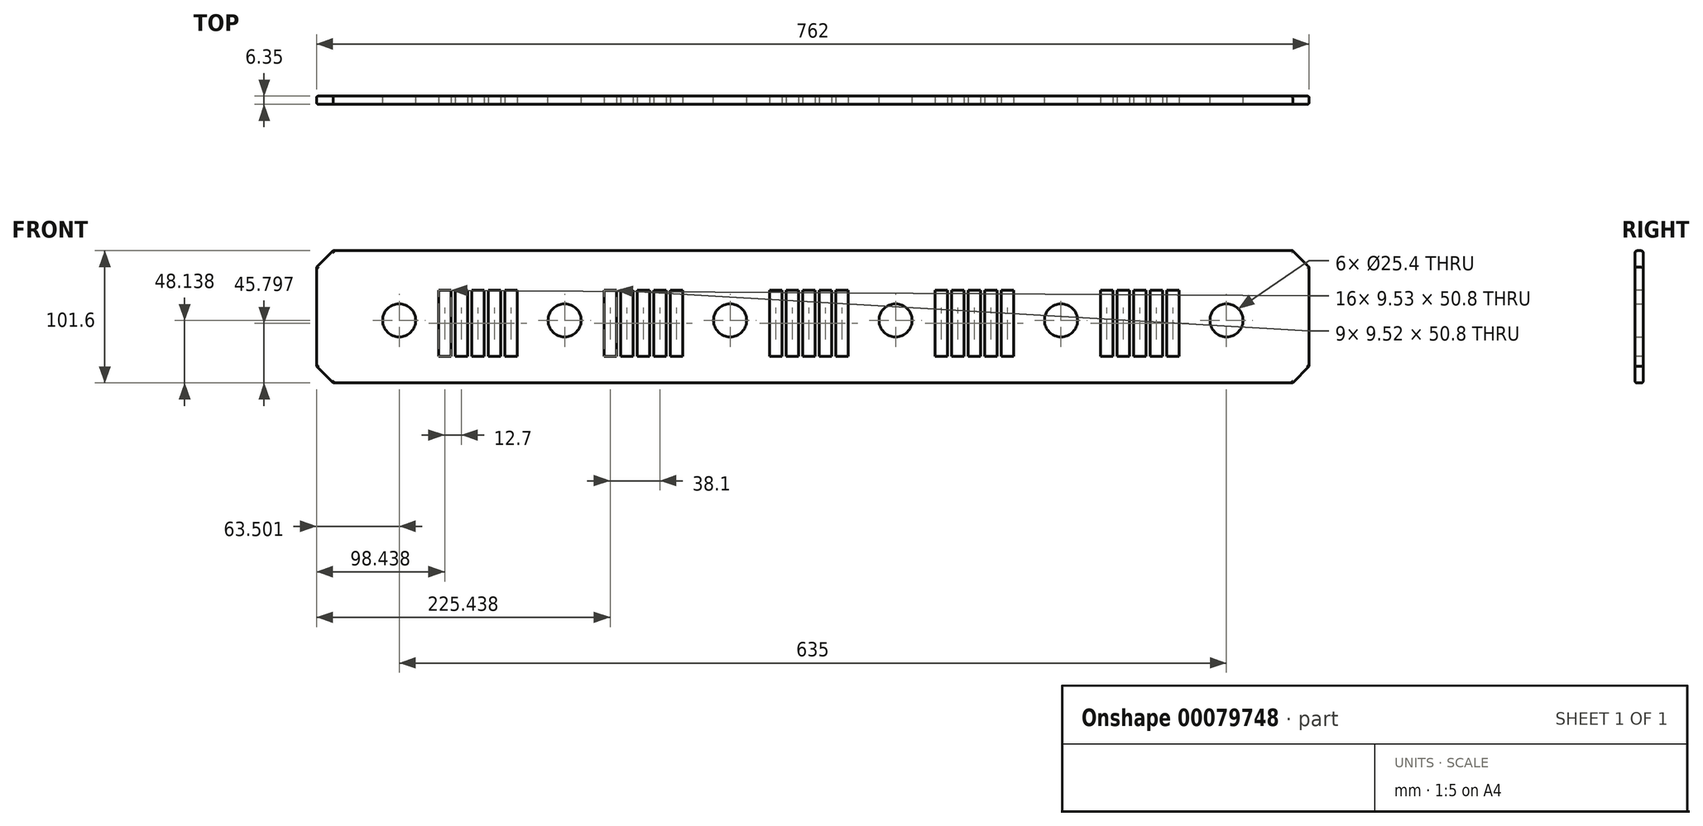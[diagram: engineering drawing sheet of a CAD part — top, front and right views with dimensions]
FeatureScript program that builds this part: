
annotation { "Feature Type Name" : "Feature", "Feature Type Description" : "" }
export const myFeature = defineFeature(function(context is Context, id is Id, definition is map)
    precondition{}
    {
        {
            var Q0;
            Q0=qCreatedBy(makeId("Front.planeOp"),FACE);
            var sketch = newSketch(context, id + "F0", { "sketchPlane" : qUnion([Q0])});
            skLineSegment(sketch, "E0.bottom", {"start": v(-361.59, -20.97) * mm, "end": v(400.41, -20.97) * mm});
            skLineSegment(sketch, "E0.top", {"start": v(-361.59, -122.57) * mm, "end": v(400.41, -122.57) * mm});
            skLineSegment(sketch, "E0.left", {"start": v(-361.59, -20.97) * mm, "end": v(-361.59, -122.57) * mm});
            skLineSegment(sketch, "E0.right", {"start": v(400.41, -20.97) * mm, "end": v(400.41, -122.57) * mm});
            skCircle(sketch, "E1", {"center": v(-298.09, -74.43) * mm, "radius": 12.7 * mm});
            skCircle(sketch, "E2", {"center": v(-171.09, -74.43) * mm, "radius": 12.7 * mm});
            skCircle(sketch, "E3", {"center": v(-44.09, -74.43) * mm, "radius": 12.7 * mm});
            skCircle(sketch, "E4", {"center": v(82.91, -74.43) * mm, "radius": 12.7 * mm});
            skCircle(sketch, "E5", {"center": v(209.91, -74.43) * mm, "radius": 12.7 * mm});
            skCircle(sketch, "E6", {"center": v(336.91, -74.43) * mm, "radius": 12.7 * mm});
            skSolve(sketch);
        }
        {
            var Q0;
            Q0 = qSketchRegion(id + "F0", true);
            extrude(context, id + "F1", {"entities" : qUnion([Q0]), "depth" : 6.35 * mm});
        }
        {
            var Q0;
            Q0=makeQuery(id+"F1.opExtrude","CAP_FACE",FACE,{"disambiguationData":[OSD([sQuery(id+"F0.wireOp",EDGE,"E0.bottom"),sQuery(id+"F0.wireOp",EDGE,"E0.top"),sQuery(id+"F0.wireOp",EDGE,"E0.left"),sQuery(id+"F0.wireOp",EDGE,"E0.right"),sQuery(id+"F0.wireOp",EDGE,"E1"),sQuery(id+"F0.wireOp",EDGE,"E2"),sQuery(id+"F0.wireOp",EDGE,"E3"),sQuery(id+"F0.wireOp",EDGE,"E4"),sQuery(id+"F0.wireOp",EDGE,"E5"),sQuery(id+"F0.wireOp",EDGE,"E6")])],"isStart":false});
            var sketch = newSketch(context, id + "F2", { "sketchPlane" : qUnion([Q0])});
            skLineSegment(sketch, "E7.bottom", {"start": v(-267.91, -51.37) * mm, "end": v(-258.39, -51.37) * mm});
            skLineSegment(sketch, "E7.top", {"start": v(-267.91, -102.17) * mm, "end": v(-258.39, -102.17) * mm});
            skLineSegment(sketch, "E7.left", {"start": v(-267.91, -51.37) * mm, "end": v(-267.91, -102.17) * mm});
            skLineSegment(sketch, "E7.right", {"start": v(-258.39, -51.37) * mm, "end": v(-258.39, -102.17) * mm});
            skLineSegment(sketch, "E8.1.0.0", {"start": v(-255.21, -51.37) * mm, "end": v(-255.21, -102.17) * mm});
            skLineSegment(sketch, "E8.1.0.1", {"start": v(-255.21, -51.37) * mm, "end": v(-245.69, -51.37) * mm});
            skLineSegment(sketch, "E8.1.0.2", {"start": v(-245.69, -51.37) * mm, "end": v(-245.69, -102.17) * mm});
            skLineSegment(sketch, "E8.1.0.3", {"start": v(-255.21, -102.17) * mm, "end": v(-245.69, -102.17) * mm});
            skLineSegment(sketch, "E8.2.0.0", {"start": v(-242.51, -51.37) * mm, "end": v(-242.51, -102.17) * mm});
            skLineSegment(sketch, "E8.2.0.1", {"start": v(-242.51, -51.37) * mm, "end": v(-232.99, -51.37) * mm});
            skLineSegment(sketch, "E8.2.0.2", {"start": v(-232.99, -51.37) * mm, "end": v(-232.99, -102.17) * mm});
            skLineSegment(sketch, "E8.2.0.3", {"start": v(-242.51, -102.17) * mm, "end": v(-232.99, -102.17) * mm});
            skLineSegment(sketch, "E8.3.0.0", {"start": v(-229.81, -51.37) * mm, "end": v(-229.81, -102.17) * mm});
            skLineSegment(sketch, "E8.3.0.1", {"start": v(-229.81, -51.37) * mm, "end": v(-220.29, -51.37) * mm});
            skLineSegment(sketch, "E8.3.0.2", {"start": v(-220.29, -51.37) * mm, "end": v(-220.29, -102.17) * mm});
            skLineSegment(sketch, "E8.3.0.3", {"start": v(-229.81, -102.17) * mm, "end": v(-220.29, -102.17) * mm});
            skLineSegment(sketch, "E8.4.0.0", {"start": v(-217.11, -51.37) * mm, "end": v(-217.11, -102.17) * mm});
            skLineSegment(sketch, "E8.4.0.1", {"start": v(-217.11, -51.37) * mm, "end": v(-207.59, -51.37) * mm});
            skLineSegment(sketch, "E8.4.0.2", {"start": v(-207.59, -51.37) * mm, "end": v(-207.59, -102.17) * mm});
            skLineSegment(sketch, "E8.4.0.3", {"start": v(-217.11, -102.17) * mm, "end": v(-207.59, -102.17) * mm});
            skLineSegment(sketch, "E8.direction1", {"start": v(-267.91, -102.17) * mm, "end": v(-255.21, -102.17) * mm, "construction": true});
            skLineSegment(sketch, "E9.bottom", {"start": v(-140.91, -51.37) * mm, "end": v(-131.39, -51.37) * mm});
            skLineSegment(sketch, "E9.top", {"start": v(-140.91, -102.17) * mm, "end": v(-131.39, -102.17) * mm});
            skLineSegment(sketch, "E9.left", {"start": v(-140.91, -51.37) * mm, "end": v(-140.91, -102.17) * mm});
            skLineSegment(sketch, "E9.right", {"start": v(-131.39, -51.37) * mm, "end": v(-131.39, -102.17) * mm});
            skLineSegment(sketch, "E10.1.0.0", {"start": v(-128.21, -51.37) * mm, "end": v(-118.69, -51.37) * mm});
            skLineSegment(sketch, "E10.1.0.1", {"start": v(-118.69, -51.37) * mm, "end": v(-118.69, -102.17) * mm});
            skLineSegment(sketch, "E10.1.0.2", {"start": v(-128.21, -51.37) * mm, "end": v(-128.21, -102.17) * mm});
            skLineSegment(sketch, "E10.1.0.3", {"start": v(-128.21, -102.17) * mm, "end": v(-118.69, -102.17) * mm});
            skLineSegment(sketch, "E10.2.0.0", {"start": v(-115.51, -51.37) * mm, "end": v(-105.99, -51.37) * mm});
            skLineSegment(sketch, "E10.2.0.1", {"start": v(-105.99, -51.37) * mm, "end": v(-105.99, -102.17) * mm});
            skLineSegment(sketch, "E10.2.0.2", {"start": v(-115.51, -51.37) * mm, "end": v(-115.51, -102.17) * mm});
            skLineSegment(sketch, "E10.2.0.3", {"start": v(-115.51, -102.17) * mm, "end": v(-105.99, -102.17) * mm});
            skLineSegment(sketch, "E10.3.0.0", {"start": v(-102.81, -51.37) * mm, "end": v(-93.29, -51.37) * mm});
            skLineSegment(sketch, "E10.3.0.1", {"start": v(-93.29, -51.37) * mm, "end": v(-93.29, -102.17) * mm});
            skLineSegment(sketch, "E10.3.0.2", {"start": v(-102.81, -51.37) * mm, "end": v(-102.81, -102.17) * mm});
            skLineSegment(sketch, "E10.3.0.3", {"start": v(-102.81, -102.17) * mm, "end": v(-93.29, -102.17) * mm});
            skLineSegment(sketch, "E10.4.0.0", {"start": v(-90.11, -51.37) * mm, "end": v(-80.59, -51.37) * mm});
            skLineSegment(sketch, "E10.4.0.1", {"start": v(-80.59, -51.37) * mm, "end": v(-80.59, -102.17) * mm});
            skLineSegment(sketch, "E10.4.0.2", {"start": v(-90.11, -51.37) * mm, "end": v(-90.11, -102.17) * mm});
            skLineSegment(sketch, "E10.4.0.3", {"start": v(-90.11, -102.17) * mm, "end": v(-80.59, -102.17) * mm});
            skLineSegment(sketch, "E10.direction1", {"start": v(-140.91, -51.37) * mm, "end": v(-128.21, -51.37) * mm, "construction": true});
            skLineSegment(sketch, "E11.bottom", {"start": v(-13.91, -51.37) * mm, "end": v(-4.39, -51.37) * mm});
            skLineSegment(sketch, "E11.top", {"start": v(-13.91, -102.17) * mm, "end": v(-4.39, -102.17) * mm});
            skLineSegment(sketch, "E11.left", {"start": v(-13.91, -51.37) * mm, "end": v(-13.91, -102.17) * mm});
            skLineSegment(sketch, "E11.right", {"start": v(-4.39, -51.37) * mm, "end": v(-4.39, -102.17) * mm});
            skLineSegment(sketch, "E12.1.0.0", {"start": v(8.31, -51.37) * mm, "end": v(8.31, -102.17) * mm});
            skLineSegment(sketch, "E12.1.0.1", {"start": v(-1.21, -51.37) * mm, "end": v(-1.21, -102.17) * mm});
            skLineSegment(sketch, "E12.1.0.2", {"start": v(-1.21, -102.17) * mm, "end": v(8.31, -102.17) * mm});
            skLineSegment(sketch, "E12.1.0.3", {"start": v(-1.21, -51.37) * mm, "end": v(8.31, -51.37) * mm});
            skLineSegment(sketch, "E12.2.0.0", {"start": v(21.01, -51.37) * mm, "end": v(21.01, -102.17) * mm});
            skLineSegment(sketch, "E12.2.0.1", {"start": v(11.49, -51.37) * mm, "end": v(11.49, -102.17) * mm});
            skLineSegment(sketch, "E12.2.0.2", {"start": v(11.49, -102.17) * mm, "end": v(21.01, -102.17) * mm});
            skLineSegment(sketch, "E12.2.0.3", {"start": v(11.49, -51.37) * mm, "end": v(21.01, -51.37) * mm});
            skLineSegment(sketch, "E12.3.0.0", {"start": v(33.71, -51.37) * mm, "end": v(33.71, -102.17) * mm});
            skLineSegment(sketch, "E12.3.0.1", {"start": v(24.19, -51.37) * mm, "end": v(24.19, -102.17) * mm});
            skLineSegment(sketch, "E12.3.0.2", {"start": v(24.19, -102.17) * mm, "end": v(33.71, -102.17) * mm});
            skLineSegment(sketch, "E12.3.0.3", {"start": v(24.19, -51.37) * mm, "end": v(33.71, -51.37) * mm});
            skLineSegment(sketch, "E12.4.0.0", {"start": v(46.41, -51.37) * mm, "end": v(46.41, -102.17) * mm});
            skLineSegment(sketch, "E12.4.0.1", {"start": v(36.89, -51.37) * mm, "end": v(36.89, -102.17) * mm});
            skLineSegment(sketch, "E12.4.0.2", {"start": v(36.89, -102.17) * mm, "end": v(46.41, -102.17) * mm});
            skLineSegment(sketch, "E12.4.0.3", {"start": v(36.89, -51.37) * mm, "end": v(46.41, -51.37) * mm});
            skLineSegment(sketch, "E12.direction1", {"start": v(-4.39, -102.17) * mm, "end": v(8.31, -102.17) * mm, "construction": true});
            skLineSegment(sketch, "E13.bottom", {"start": v(113.09, -51.37) * mm, "end": v(122.61, -51.37) * mm});
            skLineSegment(sketch, "E13.top", {"start": v(113.09, -102.17) * mm, "end": v(122.61, -102.17) * mm});
            skLineSegment(sketch, "E13.left", {"start": v(113.09, -51.37) * mm, "end": v(113.09, -102.17) * mm});
            skLineSegment(sketch, "E13.right", {"start": v(122.61, -51.37) * mm, "end": v(122.61, -102.17) * mm});
            skLineSegment(sketch, "E14.1.0.0", {"start": v(135.31, -51.37) * mm, "end": v(135.31, -102.17) * mm});
            skLineSegment(sketch, "E14.1.0.1", {"start": v(125.79, -51.37) * mm, "end": v(135.31, -51.37) * mm});
            skLineSegment(sketch, "E14.1.0.2", {"start": v(125.79, -51.37) * mm, "end": v(125.79, -102.17) * mm});
            skLineSegment(sketch, "E14.1.0.3", {"start": v(125.79, -102.17) * mm, "end": v(135.31, -102.17) * mm});
            skLineSegment(sketch, "E14.2.0.0", {"start": v(148.01, -51.37) * mm, "end": v(148.01, -102.17) * mm});
            skLineSegment(sketch, "E14.2.0.1", {"start": v(138.49, -51.37) * mm, "end": v(148.01, -51.37) * mm});
            skLineSegment(sketch, "E14.2.0.2", {"start": v(138.49, -51.37) * mm, "end": v(138.49, -102.17) * mm});
            skLineSegment(sketch, "E14.2.0.3", {"start": v(138.49, -102.17) * mm, "end": v(148.01, -102.17) * mm});
            skLineSegment(sketch, "E14.3.0.0", {"start": v(160.71, -51.37) * mm, "end": v(160.71, -102.17) * mm});
            skLineSegment(sketch, "E14.3.0.1", {"start": v(151.19, -51.37) * mm, "end": v(160.71, -51.37) * mm});
            skLineSegment(sketch, "E14.3.0.2", {"start": v(151.19, -51.37) * mm, "end": v(151.19, -102.17) * mm});
            skLineSegment(sketch, "E14.3.0.3", {"start": v(151.19, -102.17) * mm, "end": v(160.71, -102.17) * mm});
            skLineSegment(sketch, "E14.4.0.0", {"start": v(173.41, -51.37) * mm, "end": v(173.41, -102.17) * mm});
            skLineSegment(sketch, "E14.4.0.1", {"start": v(163.89, -51.37) * mm, "end": v(173.41, -51.37) * mm});
            skLineSegment(sketch, "E14.4.0.2", {"start": v(163.89, -51.37) * mm, "end": v(163.89, -102.17) * mm});
            skLineSegment(sketch, "E14.4.0.3", {"start": v(163.89, -102.17) * mm, "end": v(173.41, -102.17) * mm});
            skLineSegment(sketch, "E14.direction1", {"start": v(122.61, -102.17) * mm, "end": v(135.31, -102.17) * mm, "construction": true});
            skLineSegment(sketch, "E15.bottom", {"start": v(240.09, -51.37) * mm, "end": v(249.61, -51.37) * mm});
            skLineSegment(sketch, "E15.top", {"start": v(240.09, -102.17) * mm, "end": v(249.61, -102.17) * mm});
            skLineSegment(sketch, "E15.left", {"start": v(240.09, -51.37) * mm, "end": v(240.09, -102.17) * mm});
            skLineSegment(sketch, "E15.right", {"start": v(249.61, -51.37) * mm, "end": v(249.61, -102.17) * mm});
            skLineSegment(sketch, "E16.1.0.0", {"start": v(252.79, -51.37) * mm, "end": v(262.31, -51.37) * mm});
            skLineSegment(sketch, "E16.1.0.1", {"start": v(252.79, -51.37) * mm, "end": v(252.79, -102.17) * mm});
            skLineSegment(sketch, "E16.1.0.2", {"start": v(262.31, -51.37) * mm, "end": v(262.31, -102.17) * mm});
            skLineSegment(sketch, "E16.1.0.3", {"start": v(252.79, -102.17) * mm, "end": v(262.31, -102.17) * mm});
            skLineSegment(sketch, "E16.2.0.0", {"start": v(265.49, -51.37) * mm, "end": v(275.01, -51.37) * mm});
            skLineSegment(sketch, "E16.2.0.1", {"start": v(265.49, -51.37) * mm, "end": v(265.49, -102.17) * mm});
            skLineSegment(sketch, "E16.2.0.2", {"start": v(275.01, -51.37) * mm, "end": v(275.01, -102.17) * mm});
            skLineSegment(sketch, "E16.2.0.3", {"start": v(265.49, -102.17) * mm, "end": v(275.01, -102.17) * mm});
            skLineSegment(sketch, "E16.3.0.0", {"start": v(278.19, -51.37) * mm, "end": v(287.71, -51.37) * mm});
            skLineSegment(sketch, "E16.3.0.1", {"start": v(278.19, -51.37) * mm, "end": v(278.19, -102.17) * mm});
            skLineSegment(sketch, "E16.3.0.2", {"start": v(287.71, -51.37) * mm, "end": v(287.71, -102.17) * mm});
            skLineSegment(sketch, "E16.3.0.3", {"start": v(278.19, -102.17) * mm, "end": v(287.71, -102.17) * mm});
            skLineSegment(sketch, "E16.4.0.0", {"start": v(290.89, -51.37) * mm, "end": v(300.41, -51.37) * mm});
            skLineSegment(sketch, "E16.4.0.1", {"start": v(290.89, -51.37) * mm, "end": v(290.89, -102.17) * mm});
            skLineSegment(sketch, "E16.4.0.2", {"start": v(300.41, -51.37) * mm, "end": v(300.41, -102.17) * mm});
            skLineSegment(sketch, "E16.4.0.3", {"start": v(290.89, -102.17) * mm, "end": v(300.41, -102.17) * mm});
            skLineSegment(sketch, "E16.direction1", {"start": v(240.09, -51.37) * mm, "end": v(252.79, -51.37) * mm, "construction": true});
            skSolve(sketch);
        }
        {
            var Q0;
            Q0 = qSketchRegion(id + "F2", true);
            extrude(context, id + "F3", {"entities" : qUnion([Q0]), "operationType" : NewBodyOperationType.REMOVE, "endBound" : BoundingType.THROUGH_ALL, "oppositeDirection" : true, "depth" : 25.4 * mm});
        }
        {
            var Q0;
            Q0=makeQuery(id+"F1.opExtrude","SWEPT_EDGE",EDGE,{"disambiguationData":[OSD([sQuery(id+"F0.wireOp",EDGE,"E0.bottom"),sQuery(id+"F0.wireOp",EDGE,"E0.left")])]});
            var Q1;
            Q1=makeQuery(id+"F1.opExtrude","SWEPT_EDGE",EDGE,{"disambiguationData":[OSD([sQuery(id+"F0.wireOp",EDGE,"E0.top"),sQuery(id+"F0.wireOp",EDGE,"E0.left")])]});
            var Q2;
            Q2=makeQuery(id+"F1.opExtrude","SWEPT_EDGE",EDGE,{"disambiguationData":[OSD([sQuery(id+"F0.wireOp",EDGE,"E0.bottom"),sQuery(id+"F0.wireOp",EDGE,"E0.right")])]});
            var Q3;
            Q3=makeQuery(id+"F1.opExtrude","SWEPT_EDGE",EDGE,{"disambiguationData":[OSD([sQuery(id+"F0.wireOp",EDGE,"E0.top"),sQuery(id+"F0.wireOp",EDGE,"E0.right")])]});
            chamfer(context, id + "F4", {"entities" : qUnion([Q0, Q1, Q2, Q3]), "width" : 12.7 * mm, "tangentPropagation" : true});
        }
        {
            var Q0;
            {var subQ0=sQuery(id+"F0.wireOp",EDGE,"E0.left");var subQ1=sQuery(id+"F0.wireOp",EDGE,"E0.bottom");Q0=makeQuery(id+"F4.opChamfer","BLEND_EDGE",EDGE,{"blendedFrom":[makeQuery(id+"F1.opExtrude","SWEPT_EDGE",EDGE,{"disambiguationData":[OSD([subQ1,subQ0])]}),makeQuery(id+"F1.opExtrude","CAP_FACE",FACE,{"disambiguationData":[OSD([subQ1,sQuery(id+"F0.wireOp",EDGE,"E0.top"),subQ0,sQuery(id+"F0.wireOp",EDGE,"E0.right"),sQuery(id+"F0.wireOp",EDGE,"E1"),sQuery(id+"F0.wireOp",EDGE,"E2"),sQuery(id+"F0.wireOp",EDGE,"E3"),sQuery(id+"F0.wireOp",EDGE,"E4"),sQuery(id+"F0.wireOp",EDGE,"E5"),sQuery(id+"F0.wireOp",EDGE,"E6")])],"isStart":false})],"blendedInto":[makeQuery(id+"F1.opExtrude","CAP_FACE",FACE,{"disambiguationData":[OSD([subQ1,sQuery(id+"F0.wireOp",EDGE,"E0.top"),subQ0,sQuery(id+"F0.wireOp",EDGE,"E0.right"),sQuery(id+"F0.wireOp",EDGE,"E1"),sQuery(id+"F0.wireOp",EDGE,"E2"),sQuery(id+"F0.wireOp",EDGE,"E3"),sQuery(id+"F0.wireOp",EDGE,"E4"),sQuery(id+"F0.wireOp",EDGE,"E5"),sQuery(id+"F0.wireOp",EDGE,"E6")])],"isStart":false})]});}
            var Q1;
            Q1=makeQuery(id+"F1.opExtrude","CAP_EDGE",EDGE,{"disambiguationData":[OSD([sQuery(id+"F0.wireOp",EDGE,"E0.bottom")])],"isStart":false});
            var Q2;
            Q2=makeQuery(id+"F1.opExtrude","CAP_EDGE",EDGE,{"disambiguationData":[OSD([sQuery(id+"F0.wireOp",EDGE,"E0.bottom")])],"isStart":true});
            var Q3;
            {var subQ0=sQuery(id+"F0.wireOp",EDGE,"E0.left");var subQ1=sQuery(id+"F0.wireOp",EDGE,"E0.bottom");Q3=makeQuery(id+"F4.opChamfer","BLEND_EDGE",EDGE,{"blendedFrom":[makeQuery(id+"F1.opExtrude","SWEPT_EDGE",EDGE,{"disambiguationData":[OSD([subQ1,subQ0])]}),makeQuery(id+"F1.opExtrude","CAP_FACE",FACE,{"disambiguationData":[OSD([subQ1,sQuery(id+"F0.wireOp",EDGE,"E0.top"),subQ0,sQuery(id+"F0.wireOp",EDGE,"E0.right"),sQuery(id+"F0.wireOp",EDGE,"E1"),sQuery(id+"F0.wireOp",EDGE,"E2"),sQuery(id+"F0.wireOp",EDGE,"E3"),sQuery(id+"F0.wireOp",EDGE,"E4"),sQuery(id+"F0.wireOp",EDGE,"E5"),sQuery(id+"F0.wireOp",EDGE,"E6")])],"isStart":true})],"blendedInto":[makeQuery(id+"F1.opExtrude","CAP_FACE",FACE,{"disambiguationData":[OSD([subQ1,sQuery(id+"F0.wireOp",EDGE,"E0.top"),subQ0,sQuery(id+"F0.wireOp",EDGE,"E0.right"),sQuery(id+"F0.wireOp",EDGE,"E1"),sQuery(id+"F0.wireOp",EDGE,"E2"),sQuery(id+"F0.wireOp",EDGE,"E3"),sQuery(id+"F0.wireOp",EDGE,"E4"),sQuery(id+"F0.wireOp",EDGE,"E5"),sQuery(id+"F0.wireOp",EDGE,"E6")])],"isStart":true})]});}
            var Q4;
            Q4=makeQuery(id+"F1.opExtrude","CAP_EDGE",EDGE,{"disambiguationData":[OSD([sQuery(id+"F0.wireOp",EDGE,"E0.left")])],"isStart":true});
            var Q5;
            Q5=makeQuery(id+"F1.opExtrude","CAP_EDGE",EDGE,{"disambiguationData":[OSD([sQuery(id+"F0.wireOp",EDGE,"E0.left")])],"isStart":false});
            var Q6;
            {var subQ0=sQuery(id+"F0.wireOp",EDGE,"E0.left");var subQ1=sQuery(id+"F0.wireOp",EDGE,"E0.top");Q6=makeQuery(id+"F4.opChamfer","BLEND_EDGE",EDGE,{"blendedFrom":[makeQuery(id+"F1.opExtrude","SWEPT_EDGE",EDGE,{"disambiguationData":[OSD([subQ1,subQ0])]}),makeQuery(id+"F1.opExtrude","CAP_FACE",FACE,{"disambiguationData":[OSD([sQuery(id+"F0.wireOp",EDGE,"E0.bottom"),subQ1,subQ0,sQuery(id+"F0.wireOp",EDGE,"E0.right"),sQuery(id+"F0.wireOp",EDGE,"E1"),sQuery(id+"F0.wireOp",EDGE,"E2"),sQuery(id+"F0.wireOp",EDGE,"E3"),sQuery(id+"F0.wireOp",EDGE,"E4"),sQuery(id+"F0.wireOp",EDGE,"E5"),sQuery(id+"F0.wireOp",EDGE,"E6")])],"isStart":true})],"blendedInto":[makeQuery(id+"F1.opExtrude","CAP_FACE",FACE,{"disambiguationData":[OSD([sQuery(id+"F0.wireOp",EDGE,"E0.bottom"),subQ1,subQ0,sQuery(id+"F0.wireOp",EDGE,"E0.right"),sQuery(id+"F0.wireOp",EDGE,"E1"),sQuery(id+"F0.wireOp",EDGE,"E2"),sQuery(id+"F0.wireOp",EDGE,"E3"),sQuery(id+"F0.wireOp",EDGE,"E4"),sQuery(id+"F0.wireOp",EDGE,"E5"),sQuery(id+"F0.wireOp",EDGE,"E6")])],"isStart":true})]});}
            var Q7;
            {var subQ0=sQuery(id+"F0.wireOp",EDGE,"E0.left");var subQ1=sQuery(id+"F0.wireOp",EDGE,"E0.top");Q7=makeQuery(id+"F4.opChamfer","BLEND_EDGE",EDGE,{"blendedFrom":[makeQuery(id+"F1.opExtrude","SWEPT_EDGE",EDGE,{"disambiguationData":[OSD([subQ1,subQ0])]}),makeQuery(id+"F1.opExtrude","CAP_FACE",FACE,{"disambiguationData":[OSD([sQuery(id+"F0.wireOp",EDGE,"E0.bottom"),subQ1,subQ0,sQuery(id+"F0.wireOp",EDGE,"E0.right"),sQuery(id+"F0.wireOp",EDGE,"E1"),sQuery(id+"F0.wireOp",EDGE,"E2"),sQuery(id+"F0.wireOp",EDGE,"E3"),sQuery(id+"F0.wireOp",EDGE,"E4"),sQuery(id+"F0.wireOp",EDGE,"E5"),sQuery(id+"F0.wireOp",EDGE,"E6")])],"isStart":false})],"blendedInto":[makeQuery(id+"F1.opExtrude","CAP_FACE",FACE,{"disambiguationData":[OSD([sQuery(id+"F0.wireOp",EDGE,"E0.bottom"),subQ1,subQ0,sQuery(id+"F0.wireOp",EDGE,"E0.right"),sQuery(id+"F0.wireOp",EDGE,"E1"),sQuery(id+"F0.wireOp",EDGE,"E2"),sQuery(id+"F0.wireOp",EDGE,"E3"),sQuery(id+"F0.wireOp",EDGE,"E4"),sQuery(id+"F0.wireOp",EDGE,"E5"),sQuery(id+"F0.wireOp",EDGE,"E6")])],"isStart":false})]});}
            var Q8;
            Q8=makeQuery(id+"F1.opExtrude","CAP_EDGE",EDGE,{"disambiguationData":[OSD([sQuery(id+"F0.wireOp",EDGE,"E0.top")])],"isStart":true});
            var Q9;
            Q9=makeQuery(id+"F1.opExtrude","CAP_EDGE",EDGE,{"disambiguationData":[OSD([sQuery(id+"F0.wireOp",EDGE,"E0.top")])],"isStart":false});
            var Q10;
            {var subQ0=sQuery(id+"F0.wireOp",EDGE,"E0.right");var subQ1=sQuery(id+"F0.wireOp",EDGE,"E0.bottom");Q10=makeQuery(id+"F4.opChamfer","BLEND_EDGE",EDGE,{"blendedFrom":[makeQuery(id+"F1.opExtrude","SWEPT_EDGE",EDGE,{"disambiguationData":[OSD([subQ1,subQ0])]}),makeQuery(id+"F1.opExtrude","CAP_FACE",FACE,{"disambiguationData":[OSD([subQ1,sQuery(id+"F0.wireOp",EDGE,"E0.top"),sQuery(id+"F0.wireOp",EDGE,"E0.left"),subQ0,sQuery(id+"F0.wireOp",EDGE,"E1"),sQuery(id+"F0.wireOp",EDGE,"E2"),sQuery(id+"F0.wireOp",EDGE,"E3"),sQuery(id+"F0.wireOp",EDGE,"E4"),sQuery(id+"F0.wireOp",EDGE,"E5"),sQuery(id+"F0.wireOp",EDGE,"E6")])],"isStart":true})],"blendedInto":[makeQuery(id+"F1.opExtrude","CAP_FACE",FACE,{"disambiguationData":[OSD([subQ1,sQuery(id+"F0.wireOp",EDGE,"E0.top"),sQuery(id+"F0.wireOp",EDGE,"E0.left"),subQ0,sQuery(id+"F0.wireOp",EDGE,"E1"),sQuery(id+"F0.wireOp",EDGE,"E2"),sQuery(id+"F0.wireOp",EDGE,"E3"),sQuery(id+"F0.wireOp",EDGE,"E4"),sQuery(id+"F0.wireOp",EDGE,"E5"),sQuery(id+"F0.wireOp",EDGE,"E6")])],"isStart":true})]});}
            var Q11;
            Q11=makeQuery(id+"F1.opExtrude","CAP_EDGE",EDGE,{"disambiguationData":[OSD([sQuery(id+"F0.wireOp",EDGE,"E0.right")])],"isStart":false});
            var Q12;
            Q12=makeQuery(id+"F1.opExtrude","CAP_EDGE",EDGE,{"disambiguationData":[OSD([sQuery(id+"F0.wireOp",EDGE,"E0.right")])],"isStart":true});
            var Q13;
            {var subQ0=sQuery(id+"F0.wireOp",EDGE,"E0.right");var subQ1=sQuery(id+"F0.wireOp",EDGE,"E0.top");Q13=makeQuery(id+"F4.opChamfer","BLEND_EDGE",EDGE,{"blendedFrom":[makeQuery(id+"F1.opExtrude","SWEPT_EDGE",EDGE,{"disambiguationData":[OSD([subQ1,subQ0])]}),makeQuery(id+"F1.opExtrude","CAP_FACE",FACE,{"disambiguationData":[OSD([sQuery(id+"F0.wireOp",EDGE,"E0.bottom"),subQ1,sQuery(id+"F0.wireOp",EDGE,"E0.left"),subQ0,sQuery(id+"F0.wireOp",EDGE,"E1"),sQuery(id+"F0.wireOp",EDGE,"E2"),sQuery(id+"F0.wireOp",EDGE,"E3"),sQuery(id+"F0.wireOp",EDGE,"E4"),sQuery(id+"F0.wireOp",EDGE,"E5"),sQuery(id+"F0.wireOp",EDGE,"E6")])],"isStart":true})],"blendedInto":[makeQuery(id+"F1.opExtrude","CAP_FACE",FACE,{"disambiguationData":[OSD([sQuery(id+"F0.wireOp",EDGE,"E0.bottom"),subQ1,sQuery(id+"F0.wireOp",EDGE,"E0.left"),subQ0,sQuery(id+"F0.wireOp",EDGE,"E1"),sQuery(id+"F0.wireOp",EDGE,"E2"),sQuery(id+"F0.wireOp",EDGE,"E3"),sQuery(id+"F0.wireOp",EDGE,"E4"),sQuery(id+"F0.wireOp",EDGE,"E5"),sQuery(id+"F0.wireOp",EDGE,"E6")])],"isStart":true})]});}
            var Q14;
            {var subQ0=sQuery(id+"F0.wireOp",EDGE,"E0.right");var subQ1=sQuery(id+"F0.wireOp",EDGE,"E0.top");Q14=makeQuery(id+"F4.opChamfer","BLEND_EDGE",EDGE,{"blendedFrom":[makeQuery(id+"F1.opExtrude","SWEPT_EDGE",EDGE,{"disambiguationData":[OSD([subQ1,subQ0])]}),makeQuery(id+"F1.opExtrude","CAP_FACE",FACE,{"disambiguationData":[OSD([sQuery(id+"F0.wireOp",EDGE,"E0.bottom"),subQ1,sQuery(id+"F0.wireOp",EDGE,"E0.left"),subQ0,sQuery(id+"F0.wireOp",EDGE,"E1"),sQuery(id+"F0.wireOp",EDGE,"E2"),sQuery(id+"F0.wireOp",EDGE,"E3"),sQuery(id+"F0.wireOp",EDGE,"E4"),sQuery(id+"F0.wireOp",EDGE,"E5"),sQuery(id+"F0.wireOp",EDGE,"E6")])],"isStart":false})],"blendedInto":[makeQuery(id+"F1.opExtrude","CAP_FACE",FACE,{"disambiguationData":[OSD([sQuery(id+"F0.wireOp",EDGE,"E0.bottom"),subQ1,sQuery(id+"F0.wireOp",EDGE,"E0.left"),subQ0,sQuery(id+"F0.wireOp",EDGE,"E1"),sQuery(id+"F0.wireOp",EDGE,"E2"),sQuery(id+"F0.wireOp",EDGE,"E3"),sQuery(id+"F0.wireOp",EDGE,"E4"),sQuery(id+"F0.wireOp",EDGE,"E5"),sQuery(id+"F0.wireOp",EDGE,"E6")])],"isStart":false})]});}
            fillet(context, id + "F5", {"entities" : qUnion([Q0, Q1, Q2, Q3, Q4, Q5, Q6, Q7, Q8, Q9, Q10, Q11, Q12, Q13, Q14]), "radius" : 1.6 * mm, "tangentPropagation" : true, "allowEdgeOverflow" : false});
        }
    });
